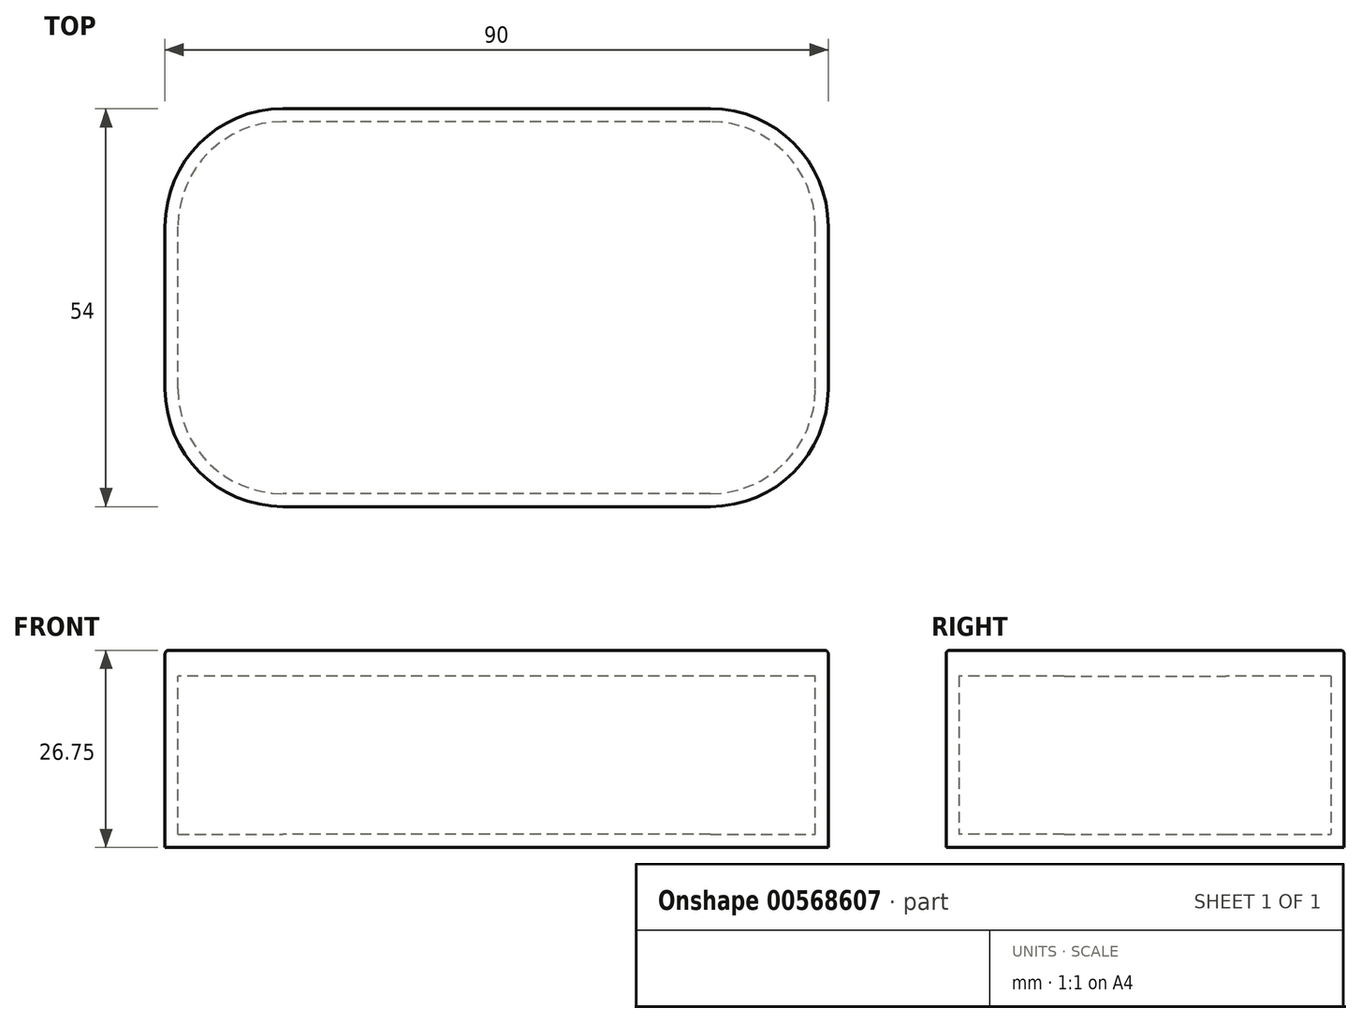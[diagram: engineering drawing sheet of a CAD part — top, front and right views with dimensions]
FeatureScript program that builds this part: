
annotation { "Feature Type Name" : "Feature", "Feature Type Description" : "" }
export const myFeature = defineFeature(function(context is Context, id is Id, definition is map)
    precondition{}
    {
        {
            var Q0;
            Q0=qCreatedBy(makeId("Top.planeOp"),FACE);
            var sketch = newSketch(context, id + "F0", { "sketchPlane" : qUnion([Q0])});
            skLineSegment(sketch, "E0.bottom", {"start": v(45, -27) * mm, "end": v(-45, -27) * mm});
            skLineSegment(sketch, "E0.top", {"start": v(45, 27) * mm, "end": v(-45, 27) * mm});
            skLineSegment(sketch, "E0.left", {"start": v(45, -27) * mm, "end": v(45, 27) * mm});
            skLineSegment(sketch, "E0.right", {"start": v(-45, -27) * mm, "end": v(-45, 27) * mm});
            skPoint(sketch, "E0.middle", {"position": v(0, 0) * mm});
            skSolve(sketch);
        }
        {
            var Q0;
            Q0 = qSketchRegion(id + "F0", true);
            extrude(context, id + "F1", {"entities" : qUnion([Q0]), "depth" : 25 * mm, "offsetDistance" : 25 * mm});
        }
        {
            var Q0;
            Q0=makeQuery(id+"F1.opExtrude","SWEPT_EDGE",EDGE,{"disambiguationData":[OSD([sQuery(id+"F0.wireOp",EDGE,"E0.bottom"),sQuery(id+"F0.wireOp",EDGE,"E0.right")])]});
            var Q1;
            Q1=makeQuery(id+"F1.opExtrude","SWEPT_EDGE",EDGE,{"disambiguationData":[OSD([sQuery(id+"F0.wireOp",EDGE,"E0.bottom"),sQuery(id+"F0.wireOp",EDGE,"E0.left")])]});
            var Q2;
            Q2=makeQuery(id+"F1.opExtrude","SWEPT_EDGE",EDGE,{"disambiguationData":[OSD([sQuery(id+"F0.wireOp",EDGE,"E0.top"),sQuery(id+"F0.wireOp",EDGE,"E0.left")])]});
            var Q3;
            Q3=makeQuery(id+"F1.opExtrude","SWEPT_EDGE",EDGE,{"disambiguationData":[OSD([sQuery(id+"F0.wireOp",EDGE,"E0.top"),sQuery(id+"F0.wireOp",EDGE,"E0.right")])]});
            fillet(context, id + "F2", {"entities" : qUnion([Q0, Q1, Q2, Q3]), "radius" : 16 * mm, "tangentPropagation" : true, "allowEdgeOverflow" : false});
        }
        {
            var Q0;
            Q0=makeQuery(id+"F1.opExtrude","CAP_FACE",FACE,{"disambiguationData":[OSD([sQuery(id+"F0.wireOp",EDGE,"E0.bottom"),sQuery(id+"F0.wireOp",EDGE,"E0.top"),sQuery(id+"F0.wireOp",EDGE,"E0.left"),sQuery(id+"F0.wireOp",EDGE,"E0.right")])],"isStart":false});
            shell(context, id + "F3", {"entities" : qUnion([Q0]), "thickness" : 1.75 * mm});
        }
        {
            var Q0;
            Q0=makeQuery(id+"F1.opExtrude","CAP_FACE",FACE,{"disambiguationData":[OSD([sQuery(id+"F0.wireOp",EDGE,"E0.bottom"),sQuery(id+"F0.wireOp",EDGE,"E0.top"),sQuery(id+"F0.wireOp",EDGE,"E0.left"),sQuery(id+"F0.wireOp",EDGE,"E0.right")])],"isStart":false});
            var sketch = newSketch(context, id + "F4", { "sketchPlane" : qUnion([Q0])});
            skArc(sketch, "E1.0", {"start": v(29, -27) * mm, "mid": v(40.31, -22.31) * mm, "end": v(45, -11) * mm});
            skLineSegment(sketch, "E2.0", {"start": v(29, -27) * mm, "end": v(-29, -27) * mm});
            skArc(sketch, "E3.0", {"start": v(-45, -11) * mm, "mid": v(-40.31, -22.31) * mm, "end": v(-29, -27) * mm});
            skArc(sketch, "E4.MirrorCS", {"start": v(-45, 11) * mm, "mid": v(-40.31, 22.31) * mm, "end": v(-29, 27) * mm});
            skLineSegment(sketch, "E5.MirrorCS", {"start": v(29, 27) * mm, "end": v(-29, 27) * mm});
            skArc(sketch, "E6.MirrorCS", {"start": v(29, 27) * mm, "mid": v(40.31, 22.31) * mm, "end": v(45, 11) * mm});
            skLineSegment(sketch, "E7", {"start": v(-45, 11) * mm, "end": v(-45, -11) * mm});
            skLineSegment(sketch, "E8", {"start": v(45, 11) * mm, "end": v(45, -11) * mm});
            skArc(sketch, "E9.0", {"start": v(-43.25, -11) * mm, "mid": v(-39.08, -21.08) * mm, "end": v(-29, -25.25) * mm});
            skLineSegment(sketch, "E9.1", {"start": v(-43.25, 11) * mm, "end": v(-43.25, -11) * mm});
            skArc(sketch, "E9.2", {"start": v(-43.25, 11) * mm, "mid": v(-39.08, 21.08) * mm, "end": v(-29, 25.25) * mm});
            skLineSegment(sketch, "E9.3", {"start": v(29, 25.25) * mm, "end": v(-29, 25.25) * mm});
            skLineSegment(sketch, "E10.0", {"start": v(29, -25.25) * mm, "end": v(-29, -25.25) * mm});
            skArc(sketch, "E10.1", {"start": v(29, -25.25) * mm, "mid": v(39.08, -21.08) * mm, "end": v(43.25, -11) * mm});
            skLineSegment(sketch, "E10.2", {"start": v(43.25, 11) * mm, "end": v(43.25, -11) * mm});
            skArc(sketch, "E10.3", {"start": v(29, 25.25) * mm, "mid": v(39.08, 21.08) * mm, "end": v(43.25, 11) * mm});
            skSolve(sketch);
        }
        {
            var Q0;
            Q0=makeQuery(id+"F4.imprint","IMPRINT",FACE,{"disambiguationData":[TD([[makeQuery(id+"F4.imprint","IMPRINT",EDGE,{"derivedFrom":sQuery(id+"F4.wireOp",EDGE,"E9.0")}),1.0]])]});
            extrude(context, id + "F5", {"entities" : qUnion([Q0]), "oppositeDirection" : true, "depth" : 1.75 * mm, "offsetDistance" : 25 * mm});
        }
        {
            var Q0;
            Q0=makeQuery(id+"F4.imprint","IMPRINT",FACE,{"disambiguationData":[TD([[makeQuery(id+"F4.imprint","IMPRINT",EDGE,{"derivedFrom":sQuery(id+"F4.wireOp",EDGE,"E1.0")}),1.0]])]});
            var Q1;
            Q1=makeQuery(id+"F4.imprint","IMPRINT",FACE,{"disambiguationData":[TD([[makeQuery(id+"F4.imprint","IMPRINT",EDGE,{"derivedFrom":sQuery(id+"F4.wireOp",EDGE,"E9.0")}),1.0]])]});
            extrude(context, id + "F6", {"entities" : qUnion([Q0, Q1]), "operationType" : NewBodyOperationType.ADD, "depth" : 1.75 * mm, "offsetDistance" : 25 * mm});
        }
        {
            var Q0;
            Q0=makeQuery(id+"F6.opExtrude","CAP_FACE",FACE,{"disambiguationData":[OSD([sQuery(id+"F4.wireOp",EDGE,"E1.0"),sQuery(id+"F4.wireOp",EDGE,"E2.0"),sQuery(id+"F4.wireOp",EDGE,"E3.0"),sQuery(id+"F4.wireOp",EDGE,"E4.MirrorCS"),sQuery(id+"F4.wireOp",EDGE,"E5.MirrorCS"),sQuery(id+"F4.wireOp",EDGE,"E6.MirrorCS"),sQuery(id+"F4.wireOp",EDGE,"E7"),sQuery(id+"F4.wireOp",EDGE,"E8")])],"isStart":false});
            fillet(context, id + "F7", {"entities" : qUnion([Q0]), "radius" : .5 * mm, "tangentPropagation" : true, "allowEdgeOverflow" : false});
        }
    });
